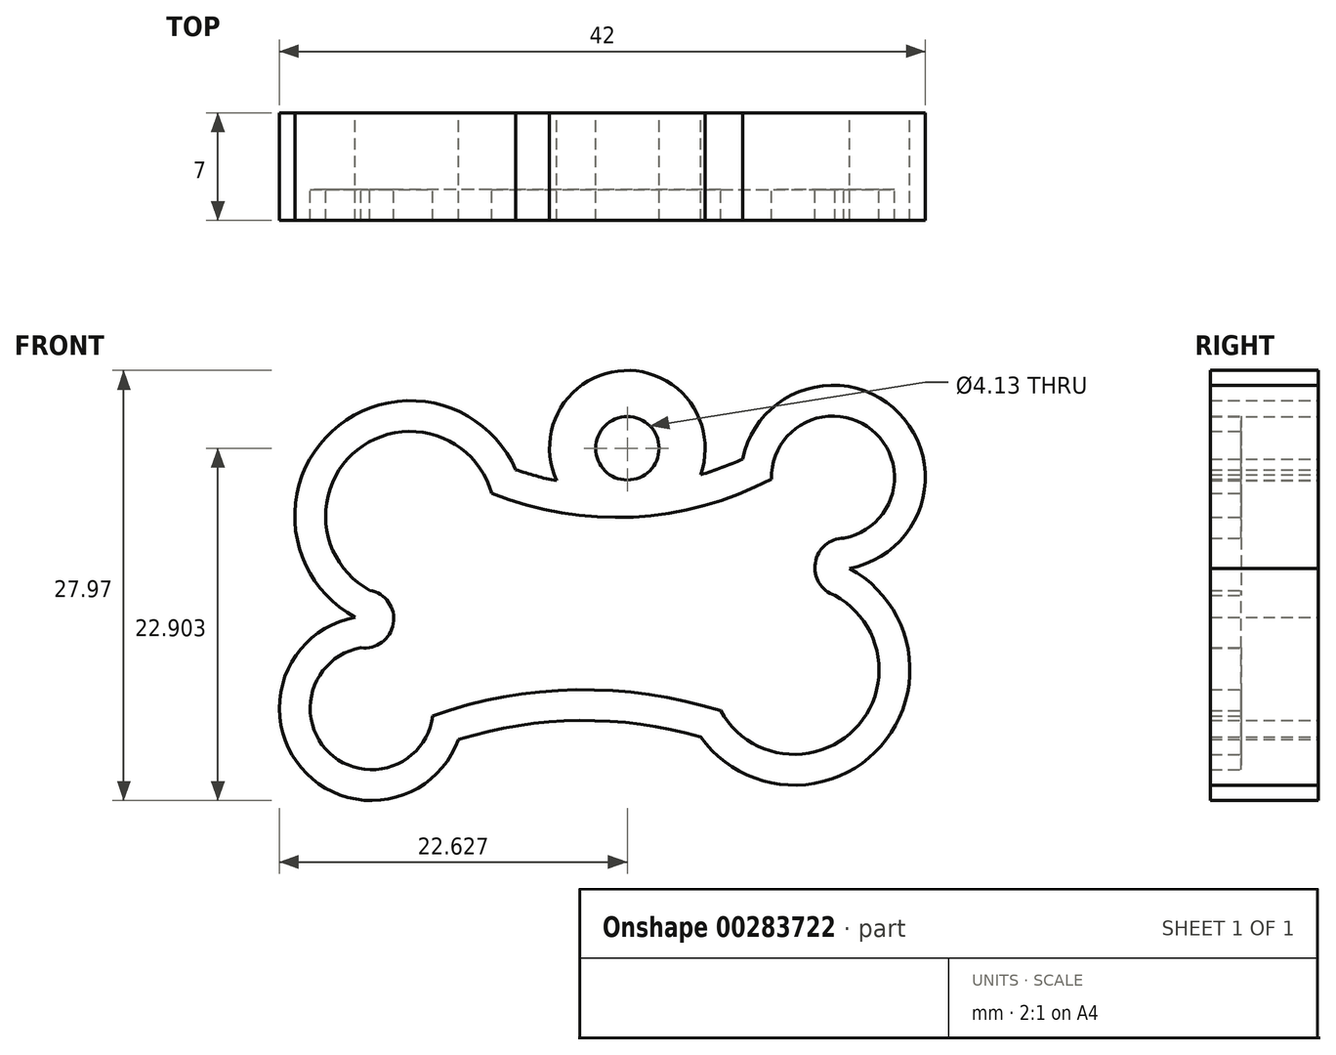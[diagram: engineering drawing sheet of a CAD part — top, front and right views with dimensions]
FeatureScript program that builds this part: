
annotation { "Feature Type Name" : "Feature", "Feature Type Description" : "" }
export const myFeature = defineFeature(function(context is Context, id is Id, definition is map)
    precondition{}
    {
        {
            var Q0;
            Q0=qCreatedBy(makeId("Front.planeOp"),FACE);
            var sketch = newSketch(context, id + "F0", { "sketchPlane" : qUnion([Q0])});
            skLineSegment(sketch, "E0.bottom", {"start": v(-20, 12.5) * mm, "end": v(20, 12.5) * mm, "construction": true});
            skLineSegment(sketch, "E0.top", {"start": v(-20, -12.5) * mm, "end": v(20, -12.5) * mm, "construction": true});
            skLineSegment(sketch, "E0.left", {"start": v(-20, 12.5) * mm, "end": v(-20, -12.5) * mm, "construction": true});
            skLineSegment(sketch, "E0.right", {"start": v(20, 12.5) * mm, "end": v(20, -12.5) * mm, "construction": true});
            skLineSegment(sketch, "E1", {"start": v(20, 12.5) * mm, "end": v(-20, -12.5) * mm, "construction": true});
            skArc(sketch, "E2", {"start": v(-5.63, 8.01) * mm, "mid": v(-17.58, 10.52) * mm, "end": v(-16.07, -1.6) * mm});
            skArc(sketch, "E3", {"start": v(6.4, -9.37) * mm, "mid": v(18.13, -9.96) * mm, "end": v(16.07, 1.6) * mm});
            skArc(sketch, "E4", {"start": v(16.07, 1.6) * mm, "mid": v(19.3, 11.7) * mm, "end": v(9.12, 8.7) * mm});
            skArc(sketch, "E5", {"start": v(-16.07, -1.6) * mm, "mid": v(-19.58, -11.37) * mm, "end": v(-9.36, -9.54) * mm});
            skArc(sketch, "E6", {"start": v(-5.63, 8.01) * mm, "mid": v(-4.32, 7.6) * mm, "end": v(-2.97, 7.29) * mm});
            skArc(sketch, "E7", {"start": v(6.4, -9.37) * mm, "mid": v(-1.5, -8.3) * mm, "end": v(-9.36, -9.54) * mm});
            skArc(sketch, "E8", {"start": v(6.4, 7.69) * mm, "mid": v(1.41, 14.46) * mm, "end": v(-2.97, 7.29) * mm});
            skCircle(sketch, "E9.converted", {"center": v(1.63, 9.4) * mm, "radius": 2.06 * mm});
            skArc(sketch, "E10.trimOffspring", {"start": v(6.4, 7.69) * mm, "mid": v(7.77, 8.14) * mm, "end": v(9.12, 8.7) * mm});
            skSolve(sketch);
        }
        {
            var Q0;
            Q0 = qSketchRegion(id + "F0", true);
            extrude(context, id + "F1", {"entities" : qUnion([Q0]), "endBound" : BoundingType.SYMMETRIC, "depth" : 5 * mm});
        }
        {
            var Q0;
            Q0=makeQuery(id+"F1.opExtrude","CAP_FACE",FACE,{"disambiguationData":[OSD([sQuery(id+"F0.wireOp",EDGE,"E2"),sQuery(id+"F0.wireOp",EDGE,"E3"),sQuery(id+"F0.wireOp",EDGE,"E4"),sQuery(id+"F0.wireOp",EDGE,"E5"),sQuery(id+"F0.wireOp",EDGE,"E6"),sQuery(id+"F0.wireOp",EDGE,"E7"),sQuery(id+"F0.wireOp",EDGE,"E8"),sQuery(id+"F0.wireOp",EDGE,"E9.converted"),sQuery(id+"F0.wireOp",EDGE,"E10.trimOffspring")])],"isStart":false});
            var sketch = newSketch(context, id + "F2", { "sketchPlane" : qUnion([Q0])});
            skArc(sketch, "E11.0", {"start": v(-7.2, 6.47) * mm, "mid": v(-15.93, 9.3) * mm, "end": v(-15.12, 0.16) * mm});
            skArc(sketch, "E12.0", {"start": v(-15.71, -3.56) * mm, "mid": v(-17.75, -10.4) * mm, "end": v(-11.03, -7.99) * mm});
            skArc(sketch, "E13.0", {"start": v(7.69, -7.67) * mm, "mid": v(-1.7, -6.3) * mm, "end": v(-11.03, -7.99) * mm});
            skArc(sketch, "E14.0", {"start": v(-7.2, 6.47) * mm, "mid": v(-0.18, 4.93) * mm, "end": v(6.95, 5.77) * mm});
            skArc(sketch, "E15.0", {"start": v(6.95, 5.77) * mm, "mid": v(9.02, 6.48) * mm, "end": v(11, 7.4) * mm});
            skArc(sketch, "E16.0", {"start": v(15.71, 3.56) * mm, "mid": v(17.52, 10.6) * mm, "end": v(11, 7.4) * mm});
            skArc(sketch, "E17.0", {"start": v(7.69, -7.67) * mm, "mid": v(16.4, -8.87) * mm, "end": v(15.12, -0.16) * mm});
            skArc(sketch, "E18", {"start": v(15.71, 3.56) * mm, "mid": v(13.84, 1.95) * mm, "end": v(15.12, -0.16) * mm});
            skArc(sketch, "E19", {"start": v(-15.71, -3.56) * mm, "mid": v(-13.6, -2) * mm, "end": v(-15.12, 0.16) * mm});
            skSolve(sketch);
        }
        {
            var Q0;
            Q0=makeQuery(id+"F2.imprint","IMPRINT",FACE,{"disambiguationData":[TD([[makeQuery(id+"F2.imprint","IMPRINT",EDGE,{"derivedFrom":sQuery(id+"F2.wireOp",EDGE,"E11.0")}),-1.0]])]});
            extrude(context, id + "F3", {"entities" : qUnion([Q0]), "operationType" : NewBodyOperationType.ADD, "depth" : 2 * mm});
        }
        {
            var Q0;
            Q0=makeQuery(id+"F1.opExtrude","CAP_FACE",FACE,{"disambiguationData":[OSD([sQuery(id+"F0.wireOp",EDGE,"E2"),sQuery(id+"F0.wireOp",EDGE,"E3"),sQuery(id+"F0.wireOp",EDGE,"E4"),sQuery(id+"F0.wireOp",EDGE,"E5"),sQuery(id+"F0.wireOp",EDGE,"E6"),sQuery(id+"F0.wireOp",EDGE,"E7"),sQuery(id+"F0.wireOp",EDGE,"E8"),sQuery(id+"F0.wireOp",EDGE,"E9.converted"),sQuery(id+"F0.wireOp",EDGE,"E10.trimOffspring")])],"isStart":false});
            var sketch = newSketch(context, id + "F4", { "sketchPlane" : qUnion([Q0])});
            skText(sketch, "E20", { "text": "PACO", "fontName": "OpenSans-Bold.ttf"});
            skText(sketch, "E21", { "text": "208 841 1140", "fontName": "OpenSans-Bold.ttf"});
            const initialGuessF4  = {"E20": [-0.01064, -0.00207, 1, 0, 0.006], "E21": [-0.01014, -0.006, 1, 0, 0.00288]};
            skSetInitialGuess(sketch, initialGuessF4);
            skSolve(sketch);
        }
        {
            var Q0;
            Q0=makeQuery(id+"F3.opExtrude","CAP_FACE",FACE,{"disambiguationData":[OSD([sQuery(id+"F0.wireOp",EDGE,"E2"),sQuery(id+"F0.wireOp",EDGE,"E3"),sQuery(id+"F0.wireOp",EDGE,"E4"),sQuery(id+"F0.wireOp",EDGE,"E5"),sQuery(id+"F0.wireOp",EDGE,"E6"),sQuery(id+"F0.wireOp",EDGE,"E7"),sQuery(id+"F0.wireOp",EDGE,"E8"),sQuery(id+"F0.wireOp",EDGE,"E9.converted"),sQuery(id+"F0.wireOp",EDGE,"E10.trimOffspring"),sQuery(id+"F2.wireOp",EDGE,"E11.0"),sQuery(id+"F2.wireOp",EDGE,"E12.0"),sQuery(id+"F2.wireOp",EDGE,"E13.0"),sQuery(id+"F2.wireOp",EDGE,"E14.0"),sQuery(id+"F2.wireOp",EDGE,"E15.0"),sQuery(id+"F2.wireOp",EDGE,"E16.0"),sQuery(id+"F2.wireOp",EDGE,"E17.0"),sQuery(id+"F2.wireOp",EDGE,"E18"),sQuery(id+"F2.wireOp",EDGE,"E19")])],"isStart":false});
            var sketch = newSketch(context, id + "F5", { "sketchPlane" : qUnion([Q0])});
            skPoint(sketch, "E22", {"position": v(-16.32, -14.5) * mm});
            skLineSegment(sketch, "E23", {"start": v(-21.26, -13.5) * mm, "end": v(-1.72, -13.5) * mm});
            skSolve(sketch);
        }
    });
